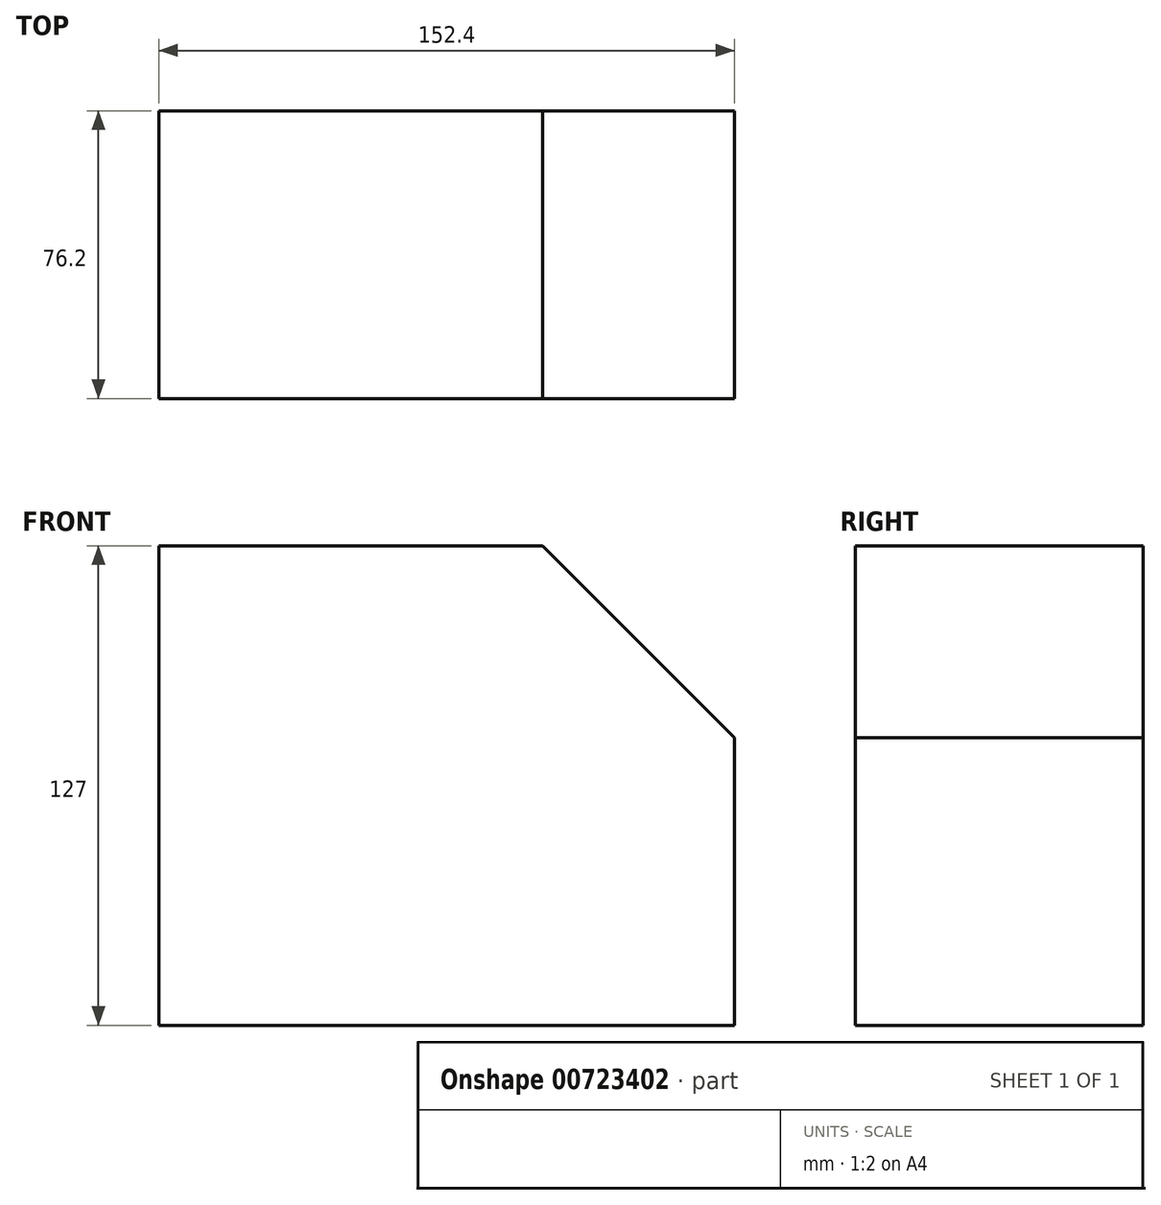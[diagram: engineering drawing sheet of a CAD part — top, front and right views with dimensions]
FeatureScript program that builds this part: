
annotation { "Feature Type Name" : "Feature", "Feature Type Description" : "" }
export const myFeature = defineFeature(function(context is Context, id is Id, definition is map)
    precondition{}
    {
        {
            var Q0;
            Q0=qCreatedBy(makeId("Front.planeOp"),FACE);
            var sketch = newSketch(context, id + "F0", { "sketchPlane" : qUnion([Q0])});
            skLineSegment(sketch, "E0", {"start": v(-92.38, -53.9) * mm, "end": v(60.02, -53.9) * mm});
            skLineSegment(sketch, "E1", {"start": v(-92.38, -53.9) * mm, "end": v(-92.38, 73.1) * mm});
            skLineSegment(sketch, "E2", {"start": v(-92.38, 73.1) * mm, "end": v(9.22, 73.1) * mm});
            skLineSegment(sketch, "E3", {"start": v(60.02, -53.9) * mm, "end": v(60.02, 22.3) * mm});
            skLineSegment(sketch, "E4", {"start": v(9.22, 73.1) * mm, "end": v(60.02, 22.3) * mm});
            skSolve(sketch);
        }
        {
            var Q0;
            Q0=makeQuery(id+"F0.imprint","IMPRINT",FACE,{"disambiguationData":[TD([[makeQuery(id+"F0.imprint","IMPRINT",EDGE,{"derivedFrom":sQuery(id+"F0.wireOp",EDGE,"E0")}),1.0]])]});
            extrude(context, id + "F1", {"entities" : qUnion([Q0]), "depth" : 76.2 * mm, "offsetDistance" : 25.4 * mm});
        }
    });
